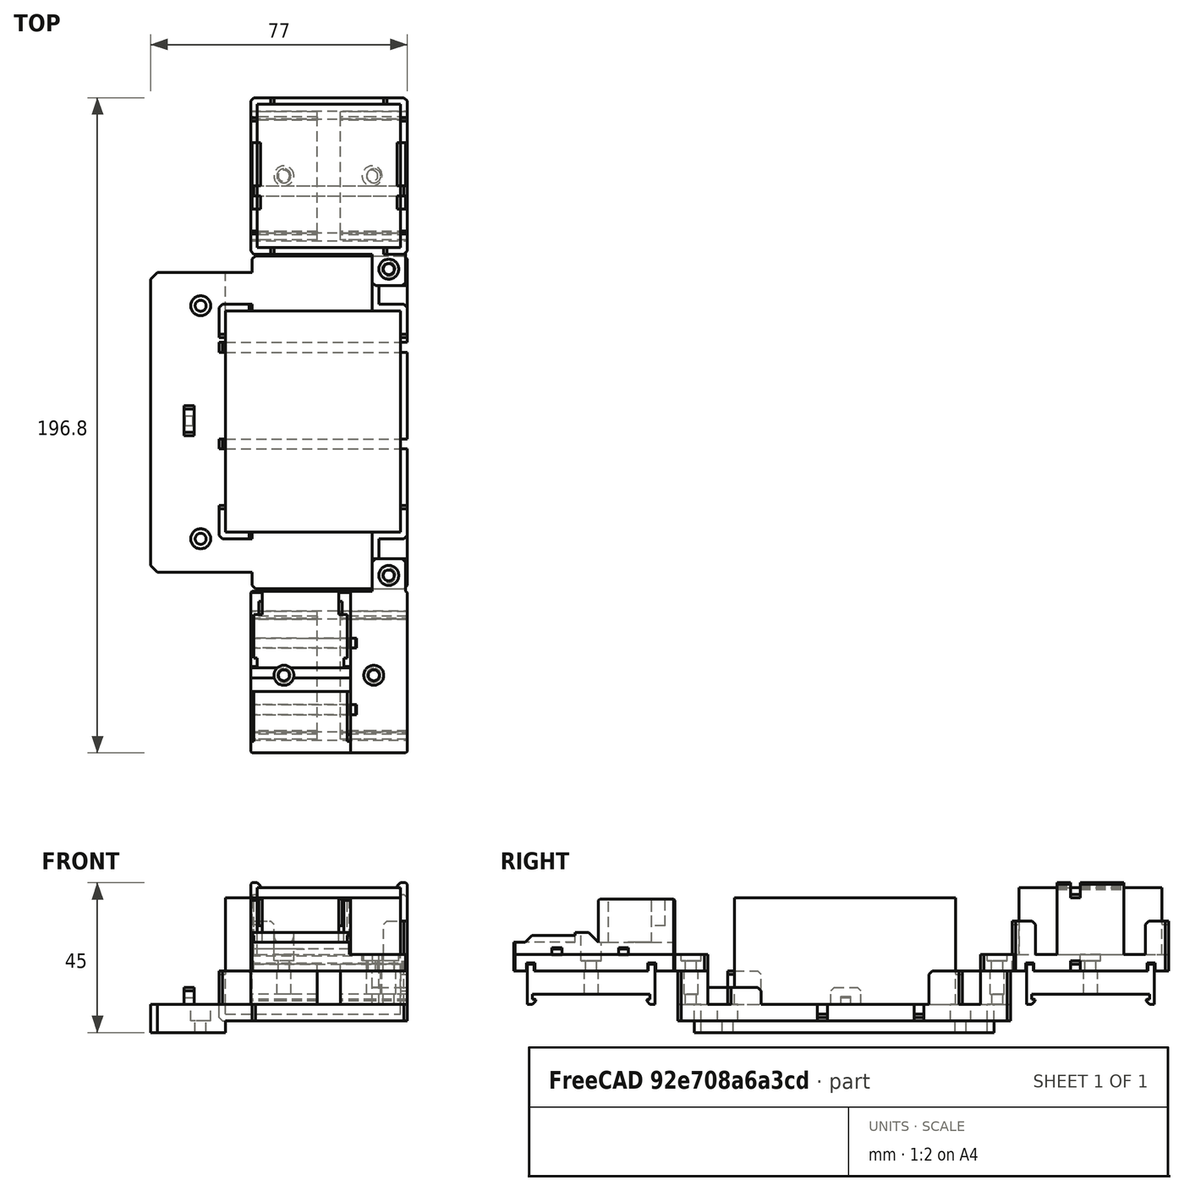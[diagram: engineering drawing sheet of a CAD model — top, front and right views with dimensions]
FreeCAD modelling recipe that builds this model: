
FCSTD DOCUMENT  (FreeCAD 0.18R16146 (Git))
Label: mini-power-power-mount
License: All rights reserved
LicenseURL: http://en.wikipedia.org/wiki/All_rights_reserved
objects: Part::Box×49, Part::MultiFuse×41, Part::Chamfer×32, Part::Cylinder×22, Part::Cut×18, Part::Feature×6
note: 168 computed .brp shape members not serialized (recipe doc carries the construction recipe); baked Part::Feature solids carry a one-line shape summary decoded from their .brp

FEATURE [Part::Feature] Cut003001  label="din-mount"
  Placement = pos=(23.5,-18,-10) rot=(0,-1,0;1.5708rad)
  shape: bbox 20 x 38.4 x 12 mm, 68 faces (baked)
FEATURE [Part::Box] Box  label="sonoff-pos"
  AttacherType = Attacher::AttachEngine3D
  Height = 20
  Length = 43
  Placement = pos=(-21.5,-21.5,0) rot=(0,0,1;0rad)
  Width = 43
FEATURE [Part::Box] Box001  label="Cube"
  AttacherType = Attacher::AttachEngine3D
  Height = 10
  Length = 7
  Placement = pos=(-23.5,21.5,0) rot=(0,0,1;0rad)
  Width = 2
FEATURE [Part::Box] Box002  label="Cube001"
  AttacherType = Attacher::AttachEngine3D
  Height = 10
  Length = 7
  Placement = pos=(16.5,21.5,0) rot=(0,0,1;0rad)
  Width = 2
FEATURE [Part::Box] Box003  label="Cube002"
  AttacherType = Attacher::AttachEngine3D
  Height = 10
  Length = 7
  Placement = pos=(-23.5,-23.5,0) rot=(0,0,1;0rad)
  Width = 2
FEATURE [Part::Box] Box004  label="Cube003"
  AttacherType = Attacher::AttachEngine3D
  Height = 10
  Length = 7
  Placement = pos=(16.5,-23.5,0) rot=(0,0,1;0rad)
  Width = 2
FEATURE [Part::Box] Box005  label="Cube004"
  AttacherType = Attacher::AttachEngine3D
  Height = 10
  Length = 2
  Placement = pos=(-23.5,-23.5,0) rot=(0,0,1;0rad)
  Width = 7
FEATURE [Part::Box] Box006  label="Cube005"
  AttacherType = Attacher::AttachEngine3D
  Height = 10
  Length = 2
  Placement = pos=(21.5,-23.5,0) rot=(0,0,1;0rad)
  Width = 7
FEATURE [Part::Box] Box007  label="Cube006"
  AttacherType = Attacher::AttachEngine3D
  Height = 10
  Length = 2
  Placement = pos=(21.5,16.5,0) rot=(0,0,1;0rad)
  Width = 7
FEATURE [Part::Box] Box008  label="Cube007"
  AttacherType = Attacher::AttachEngine3D
  Height = 10
  Length = 2
  Placement = pos=(-23.5,16.5,0) rot=(0,0,1;0rad)
  Width = 7
FEATURE [Part::Feature] Cut003002  label="din-mount001"
  Placement = pos=(-3.5,-18,-10) rot=(0,-1,0;1.5708rad)
  shape: bbox 20 x 38.4 x 12 mm, 68 faces (baked)
FEATURE [Part::Box] Box009  label="Cube008"
  AttacherType = Attacher::AttachEngine3D
  Height = 20
  Length = 2
  Placement = pos=(-23.5,-10,0) rot=(0,0,1;0rad)
  Width = 20
FEATURE [Part::Box] Box010  label="Cube009"
  AttacherType = Attacher::AttachEngine3D
  Height = 20
  Length = 2
  Placement = pos=(21.5,-10,0) rot=(0,0,1;0rad)
  Width = 20
FEATURE [Part::Box] Box011  label="Cube010"
  AttacherType = Attacher::AttachEngine3D
  Height = 2
  Length = 3
  Placement = pos=(-23.5,-10,19.5) rot=(0,0,1;0rad)
  Width = 20
FEATURE [Part::Box] Box012  label="Cube011"
  AttacherType = Attacher::AttachEngine3D
  Height = 2
  Length = 3
  Placement = pos=(20.5,-10,19.5) rot=(0,0,1;0rad)
  Width = 20
FEATURE [Part::Chamfer] Chamfer
  Base = -> Box011
  Edges = 1 edges r=1: [Edge6]
FEATURE [Part::Chamfer] Chamfer001
  Base = -> Box012
  Edges = 1 edges r=1: [Edge2]
FEATURE [Part::Chamfer] Chamfer002
  Base = -> Chamfer
  Edges = 1 edges: [Edge3 r1=0.5 r2=1]
FEATURE [Part::Chamfer] Chamfer003
  Base = -> Chamfer001
  Edges = 1 edges: [Edge3 r1=0.5 r2=1]
FEATURE [Part::Chamfer] Chamfer004
  Base = -> Chamfer002
  Edges = 1 edges r=0.5: [Edge18]
FEATURE [Part::Chamfer] Chamfer005
  Base = -> Chamfer003
  Edges = 1 edges r=0.5: [Edge18]
FEATURE [Part::MultiFuse] Fusion
  Shapes = -> [Box009,Chamfer004]
FEATURE [Part::MultiFuse] Fusion001
  Shapes = -> [Box010,Chamfer005]
FEATURE [Part::MultiFuse] Fusion002
  Shapes = -> [Box008,Box001]
FEATURE [Part::MultiFuse] Fusion003
  Shapes = -> [Box002,Box007]
FEATURE [Part::MultiFuse] Fusion004
  Shapes = -> [Box005,Box003]
FEATURE [Part::MultiFuse] Fusion005
  Shapes = -> [Box004,Box006]
FEATURE [Part::Chamfer] Chamfer006
  Base = -> Fusion002
  Edges = 1 edges r=1: [Edge9]
FEATURE [Part::Chamfer] Chamfer007
  Base = -> Fusion004
  Edges = 1 edges r=1: [Edge1]
FEATURE [Part::Chamfer] Chamfer008
  Base = -> Fusion005
  Edges = 1 edges r=1: [Edge14]
FEATURE [Part::Chamfer] Chamfer009
  Base = -> Fusion003
  Edges = 1 edges r=1: [Edge20]
FEATURE [Part::Box] Box013  label="Cube012"
  AttacherType = Attacher::AttachEngine3D
  Height = 5
  Length = 47
  Placement = pos=(-23.5,-23.5,-5) rot=(0,0,1;0rad)
  Width = 47
FEATURE [Part::MultiFuse] Fusion006  label="din-pos"
  Placement = pos=(0,0.3,-2) rot=(0,0,1;0rad)
  Shapes = -> [Cut003001,Cut003002]
FEATURE [Part::Cylinder] Cylinder
  Angle = 360
  AttacherType = Attacher::AttachEngine3D
  Height = 10
  Placement = pos=(-13.5,0,0) rot=(0,0,1;0rad)
  Radius = 3
FEATURE [Part::Cylinder] Cylinder001
  Angle = 360
  AttacherType = Attacher::AttachEngine3D
  Height = 10
  Placement = pos=(13,0,0) rot=(0,0,1;0rad)
  Radius = 3
FEATURE [Part::Cylinder] Cylinder002
  Angle = 360
  AttacherType = Attacher::AttachEngine3D
  Height = 10
  Placement = pos=(13,0,0) rot=(0,0,1;0rad)
  Radius = 1.7
FEATURE [Part::Cylinder] Cylinder003
  Angle = 360
  AttacherType = Attacher::AttachEngine3D
  Height = 10
  Placement = pos=(-13.5,0,0) rot=(0,0,1;0rad)
  Radius = 1.7
FEATURE [Part::MultiFuse] Fusion007
  Shapes = -> [Cylinder003,Cylinder002]
FEATURE [Part::MultiFuse] Fusion008
  Placement = pos=(0,0,10) rot=(0,0,1;0rad)
  Shapes = -> [Cylinder001,Cylinder]
FEATURE [Part::MultiFuse] Fusion009
  Placement = pos=(0,0,-12) rot=(0,0,1;0rad)
  Shapes = -> [Fusion008,Fusion007]
FEATURE [Part::Chamfer] Chamfer010
  Base = -> Box013
  Edges = 4 edges r=1: [Edge1,Edge3,Edge5,Edge7]
FEATURE [Part::Cut] Cut
  Base = -> Chamfer010
  Tool = -> Fusion009
FEATURE [Part::Box] Box014  label="Cube013"
  AttacherType = Attacher::AttachEngine3D
  Height = 2.4
  Length = 50
  Placement = pos=(-25,-19.45,-5) rot=(0,0,1;0rad)
  Width = 2.4
FEATURE [Part::Box] Box015  label="Cube014"
  AttacherType = Attacher::AttachEngine3D
  Height = 2.4
  Length = 50
  Placement = pos=(-25,17.05,-5) rot=(0,0,1;0rad)
  Width = 2.4
FEATURE [Part::MultiFuse] Fusion010
  Shapes = -> [Fusion,Fusion001,Chamfer006,Chamfer007,Chamfer008,Chamfer009,Cut]
FEATURE [Part::Chamfer] Chamfer011
  Base = -> Fusion010
  Edges = 8 edges r=1: [Edge23,Edge27,Edge90,Edge99,Edge106,Edge122,Edge129,Edge136]
FEATURE [Part::MultiFuse] Fusion011
  Shapes = -> [Box014,Box015]
FEATURE [Part::Cut] Cut003003
  Base = -> Chamfer011
  Tool = -> Fusion011
FEATURE [Part::Cylinder] Cylinder004
  Angle = 360
  AttacherType = Attacher::AttachEngine3D
  Height = 10
  Placement = pos=(18,-28,0) rot=(0,0,1;0rad)
  Radius = 3
FEATURE [Part::Box] Box016  label="Cube015"
  AttacherType = Attacher::AttachEngine3D
  Height = 5
  Length = 10
  Placement = pos=(13,-33,-5) rot=(0,0,1;0rad)
  Width = 10
FEATURE [Part::Cylinder] Cylinder005
  Angle = 360
  AttacherType = Attacher::AttachEngine3D
  Height = 10
  Placement = pos=(18,-28,-7) rot=(0,0,1;0rad)
  Radius = 1.7
FEATURE [Part::MultiFuse] Fusion012
  Placement = pos=(0,0,-2) rot=(0,0,1;0rad)
  Shapes = -> [Cylinder005,Cylinder004]
FEATURE [Part::Cut] Cut003004
  Base = -> Box016
  Tool = -> Fusion012
FEATURE [Part::Chamfer] Chamfer012
  Base = -> Cut003004
  Edges = 2 edges r=1: [Edge1,Edge6]
FEATURE [Part::MultiFuse] Fusion013  label="sonoff-r1"
  Shapes = -> [Cut003003,Chamfer012]
FEATURE [Part::Feature] Fusion006001  label="din-pos001"
  Placement = pos=(0,-149.7,-2) rot=(0,0,1;0rad)
  shape: bbox 47 x 38.4 x 12 mm, 136 faces, 2 solids (baked)
FEATURE [Part::Feature] Chamfer005001  label="power-connector-mount"
  Placement = pos=(6.5,-149.3,-0.4) rot=(0,0,1;3.14159rad)
  shape: bbox 30 x 48.5 x 17 mm, 71 faces (baked)
FEATURE [Part::Box] Box017  label="Cube016"
  AttacherType = Attacher::AttachEngine3D
  Height = 5
  Length = 47
  Placement = pos=(-23.5,-173.3,-5) rot=(0,0,1;0rad)
  Width = 48.5
FEATURE [Part::Chamfer] Chamfer005002
  Base = -> Box017
  Edges = 4 edges r=0.4: [Edge1,Edge3,Edge5,Edge7]
FEATURE [Part::MultiFuse] Fusion006002
  Shapes = -> [Chamfer005002,Chamfer005001]
FEATURE [Part::Cylinder] Cylinder006
  Angle = 360
  AttacherType = Attacher::AttachEngine3D
  Height = 15
  Placement = pos=(-13.5,-150,0) rot=(0,0,1;0rad)
  Radius = 1.65
FEATURE [Part::Cylinder] Cylinder007
  Angle = 360
  AttacherType = Attacher::AttachEngine3D
  Height = 15
  Placement = pos=(13.5,-150,0) rot=(0,0,1;0rad)
  Radius = 1.65
FEATURE [Part::Cylinder] Cylinder008
  Angle = 360
  AttacherType = Attacher::AttachEngine3D
  Height = 15
  Placement = pos=(-13.5,-150,0) rot=(0,0,1;0rad)
  Radius = 3
FEATURE [Part::Cylinder] Cylinder009
  Angle = 360
  AttacherType = Attacher::AttachEngine3D
  Height = 15
  Placement = pos=(13.5,-150,0) rot=(0,0,1;0rad)
  Radius = 3
FEATURE [Part::MultiFuse] Fusion006003
  Placement = pos=(0,0,13) rot=(0,0,1;0rad)
  Shapes = -> [Cylinder009,Cylinder008]
FEATURE [Part::MultiFuse] Fusion006004
  Shapes = -> [Cylinder007,Cylinder006]
FEATURE [Part::MultiFuse] Fusion006005
  Placement = pos=(0,0,-15) rot=(0,0,1;0rad)
  Shapes = -> [Fusion006003,Fusion006004]
FEATURE [Part::Cylinder] Cylinder010
  Angle = 360
  AttacherType = Attacher::AttachEngine3D
  Height = 4
  Placement = pos=(-8.5,-135,-0.4) rot=(0,0,1;0rad)
  Radius = 4
FEATURE [Part::Cylinder] Cylinder011
  Angle = 360
  AttacherType = Attacher::AttachEngine3D
  Height = 4
  Placement = pos=(-8.5,-154.5,-0.4) rot=(0,0,1;0rad)
  Radius = 4
FEATURE [Part::Box] Box018  label="Cube017"
  AttacherType = Attacher::AttachEngine3D
  Height = 6
  Length = 10
  Placement = pos=(-13.5,-154.8,0.6) rot=(0,0,1;0rad)
  Width = 4
FEATURE [Part::MultiFuse] Fusion006006
  Shapes = -> [Fusion006002,Cylinder010,Cylinder011,Box018]
FEATURE [Part::Cut] Cut003005
  Base = -> Fusion006006
  Tool = -> Fusion006005
FEATURE [Part::Box] Box019  label="Cube018"
  AttacherType = Attacher::AttachEngine3D
  Height = 2
  Length = 50
  Placement = pos=(-25,-141.8,-0.4) rot=(0,0,1;0rad)
  Width = 3
FEATURE [Part::Box] Box020  label="Cube019"
  AttacherType = Attacher::AttachEngine3D
  Height = 2
  Length = 50
  Placement = pos=(-25,-161.8,-0.4) rot=(0,0,1;0rad)
  Width = 3
FEATURE [Part::Box] Box021  label="Cube020"
  AttacherType = Attacher::AttachEngine3D
  Height = 2.4
  Length = 50
  Placement = pos=(-25,-133.05,-5) rot=(0,0,1;0rad)
  Width = 2.5
FEATURE [Part::MultiFuse] Fusion006007
  Placement = pos=(-17,0,0) rot=(0,0,1;0rad)
  Shapes = -> [Box019,Box020]
FEATURE [Part::Cut] Cut003006
  Base = -> Cut003005
  Tool = -> Fusion006007
FEATURE [Part::Chamfer] Chamfer005003
  Base = -> Cut003006
  Edges = 2 edges r=0.3: [Edge143,Edge146]
FEATURE [Part::Chamfer] Chamfer005004
  Base = -> Chamfer005003
  Edges = 4 edges r=0.4: [Edge30,Edge33,Edge97,Edge103]
FEATURE [Part::Box] Box022  label="Cube021"
  AttacherType = Attacher::AttachEngine3D
  Height = 2.4
  Length = 50
  Placement = pos=(-25,-169.45,-5) rot=(0,0,1;0rad)
  Width = 2.5
FEATURE [Part::Cut] Cut003007
  Base = -> Chamfer005004
  Tool = -> Box021
FEATURE [Part::Cut] Cut003008
  Base = -> Cut003007
  Tool = -> Box022
FEATURE [Part::Cylinder] Cylinder012
  Angle = 360
  AttacherType = Attacher::AttachEngine3D
  Height = 10
  Placement = pos=(18,-121,0) rot=(0,0,1;0rad)
  Radius = 3
FEATURE [Part::Cylinder] Cylinder013
  Angle = 360
  AttacherType = Attacher::AttachEngine3D
  Height = 10
  Placement = pos=(18,-121,-7) rot=(0,0,1;0rad)
  Radius = 1.65
FEATURE [Part::MultiFuse] Fusion006008
  Placement = pos=(0,0,-2) rot=(0,0,1;0rad)
  Shapes = -> [Cylinder013,Cylinder012]
FEATURE [Part::Box] Box023  label="Cube022"
  AttacherType = Attacher::AttachEngine3D
  Height = 5
  Length = 10
  Placement = pos=(13,-126,-5) rot=(0,0,1;0rad)
  Width = 10
FEATURE [Part::Chamfer] Chamfer005005
  Base = -> Box023
  Edges = 2 edges r=1: [Edge3,Edge7]
FEATURE [Part::Cut] Cut003009
  Base = -> Chamfer005005
  Placement = pos=(0,1,0) rot=(0,0,1;0rad)
  Tool = -> Fusion006008
FEATURE [Part::MultiFuse] Fusion006009  label="plug-r1"
  Shapes = -> [Cut003008,Cut003009]
FEATURE [Part::Box] Box024  label="Cube023"
  AttacherType = Attacher::AttachEngine3D
  Height = 2
  Length = 50
  Placement = pos=(-25,-6,-5) rot=(0,0,1;0rad)
  Width = 3
FEATURE [Part::Box] Box025  label="Cube024"
  AttacherType = Attacher::AttachEngine3D
  Height = 5
  Length = 50
  Placement = pos=(-25,-6,18) rot=(0,0,1;0rad)
  Width = 3
FEATURE [Part::Cut] Cut003010
  Base = -> Fusion013
  Tool = -> Box024
FEATURE [Part::Chamfer] Chamfer005006
  Base = -> Cut003010
  Edges = 2 edges r=1: [Edge28,Edge98]
FEATURE [Part::Cut] Cut003011
  Base = -> Chamfer005006
  Tool = -> Box025
FEATURE [Part::Chamfer] Chamfer005007  label="sonoff-r1-f1"
  Base = -> Cut003011
  Edges = 2 edges r=1: [Edge112,Edge255]
FEATURE [Part::Cylinder] Cylinder014
  Angle = 360
  AttacherType = Attacher::AttachEngine3D
  Height = 20
  Placement = pos=(18,-28,0) rot=(0,0,1;0rad)
  Radius = 1.65
FEATURE [Part::Cylinder] Cylinder015
  Angle = 360
  AttacherType = Attacher::AttachEngine3D
  Height = 20
  Placement = pos=(18,-120,0) rot=(0,0,1;0rad)
  Radius = 1.65
FEATURE [Part::Cylinder] Cylinder016
  Angle = 360
  AttacherType = Attacher::AttachEngine3D
  Height = 10
  Placement = pos=(-38.5,-34,0) rot=(0,0,1;0rad)
  Radius = 1.65
FEATURE [Part::Box] Box026  label="Cube025"
  AttacherType = Attacher::AttachEngine3D
  Height = 32
  Length = 52.5
  Placement = pos=(-31,-107,-15) rot=(0,0,1;0rad)
  Width = 66.5
FEATURE [Part::Box] Box027  label="Cube026"
  AttacherType = Attacher::AttachEngine3D
  Height = 5
  Length = 77
  Placement = pos=(-53.5,-124,-20) rot=(0,0,1;0rad)
  Width = 100
FEATURE [Part::Box] Box028  label="Cube027"
  AttacherType = Attacher::AttachEngine3D
  Height = 10
  Length = 10.5
  Placement = pos=(13,-33,-15) rot=(0,0,1;0rad)
  Width = 9
FEATURE [Part::Box] Box029  label="Cube028"
  AttacherType = Attacher::AttachEngine3D
  Height = 10
  Length = 10.5
  Placement = pos=(13,-124,-15) rot=(0,0,1;0rad)
  Width = 9
FEATURE [Part::Box] Box030  label="Cube029"
  AttacherType = Attacher::AttachEngine3D
  Height = 10
  Length = 10
  Placement = pos=(13.5,-40.5,-15) rot=(0,0,1;0rad)
  Width = 2
FEATURE [Part::Box] Box031  label="Cube030"
  AttacherType = Attacher::AttachEngine3D
  Height = 10
  Length = 10
  Placement = pos=(-33,-40.5,-15) rot=(0,0,1;0rad)
  Width = 2
FEATURE [Part::Box] Box032  label="Cube031"
  AttacherType = Attacher::AttachEngine3D
  Height = 10
  Length = 10
  Placement = pos=(-33,-109,-15) rot=(0,0,1;0rad)
  Width = 2
FEATURE [Part::Box] Box033  label="Cube032"
  AttacherType = Attacher::AttachEngine3D
  Height = 5
  Length = 10
  Placement = pos=(13.5,-109,-15) rot=(0,0,1;0rad)
  Width = 2
FEATURE [Part::Box] Box034  label="Cube033"
  AttacherType = Attacher::AttachEngine3D
  Height = 10
  Length = 2
  Placement = pos=(-33,-48.5,-15) rot=(0,0,1;0rad)
  Width = 10
FEATURE [Part::Box] Box035  label="Cube034"
  AttacherType = Attacher::AttachEngine3D
  Height = 10
  Length = 2
  Placement = pos=(21.5,-48.5,-15) rot=(0,0,1;0rad)
  Width = 10
FEATURE [Part::Box] Box036  label="Cube035"
  AttacherType = Attacher::AttachEngine3D
  Height = 5
  Length = 2
  Placement = pos=(21.5,-107,-15) rot=(0,0,1;0rad)
  Width = 8
FEATURE [Part::Box] Box037  label="Cube036"
  AttacherType = Attacher::AttachEngine3D
  Height = 10
  Length = 2
  Placement = pos=(-33,-109,-15) rot=(0,0,1;0rad)
  Width = 10
FEATURE [Part::MultiFuse] Fusion006010
  Shapes = -> [Box037,Box032]
FEATURE [Part::Chamfer] Chamfer005009
  Base = -> Fusion006010
  Edges = 3 edges r=1: [Edge1,Edge18,Edge21]
FEATURE [Part::MultiFuse] Fusion006013
  Shapes = -> [Box034,Box031]
FEATURE [Part::Chamfer] Chamfer005012
  Base = -> Fusion006013
  Edges = 3 edges r=1: [Edge7,Edge9,Edge22]
FEATURE [Part::Box] Box038  label="Cube037"
  AttacherType = Attacher::AttachEngine3D
  Height = 10
  Length = 2
  Placement = pos=(13,-40.5,-15) rot=(0,0,1;0rad)
  Width = 16.5
FEATURE [Part::Box] Box039  label="Cube038"
  AttacherType = Attacher::AttachEngine3D
  Height = 5
  Length = 2
  Placement = pos=(13,-124,-15) rot=(0,0,1;0rad)
  Width = 17
FEATURE [Part::MultiFuse] Fusion006015
  Shapes = -> [Box030,Box035]
FEATURE [Part::Chamfer] Chamfer005014
  Base = -> Fusion006015
  Edges = 2 edges r=1: [Edge20,Edge24]
FEATURE [Part::MultiFuse] Fusion006016
  Shapes = -> [Box038,Box028]
FEATURE [Part::Chamfer] Chamfer005015
  Base = -> Fusion006016
  Edges = 1 edges r=1: [Edge27]
FEATURE [Part::MultiFuse] Fusion006017
  Shapes = -> [Box033,Box036]
FEATURE [Part::Chamfer] Chamfer005016
  Base = -> Fusion006017
  Edges = 2 edges r=1: [Edge6,Edge17]
FEATURE [Part::Chamfer] Chamfer005017
  Base = -> Box029
  Edges = 1 edges r=1: [Edge5]
FEATURE [Part::MultiFuse] Fusion006018
  Shapes = -> [Box039,Chamfer005016,Chamfer005017]
FEATURE [Part::MultiFuse] Fusion006019
  Shapes = -> [Chamfer005015,Chamfer005014]
FEATURE [Part::MultiFuse] Fusion006020
  Shapes = -> [Chamfer005009,Fusion006018,Fusion006019,Chamfer005012]
FEATURE [Part::Cylinder] Cylinder017
  Angle = 360
  AttacherType = Attacher::AttachEngine3D
  Height = 7
  Placement = pos=(18,-28,0) rot=(0,0,1;0rad)
  Radius = 2.1
FEATURE [Part::Cylinder] Cylinder018
  Angle = 360
  AttacherType = Attacher::AttachEngine3D
  Height = 7
  Placement = pos=(18,-120,0) rot=(0,0,1;0rad)
  Radius = 2.1
FEATURE [Part::MultiFuse] Fusion006021
  Placement = pos=(0,0,-23) rot=(0,0,1;0rad)
  Shapes = -> [Cylinder014,Cylinder015]
FEATURE [Part::Cut] Cut003012
  Base = -> Fusion006020
  Tool = -> Fusion006021
FEATURE [Part::MultiFuse] Fusion006022
  Placement = pos=(0,0,-12) rot=(0,0,1;0rad)
  Shapes = -> [Cylinder018,Cylinder017]
FEATURE [Part::Cut] Cut003013
  Base = -> Cut003012
  Tool = -> Fusion006022
FEATURE [Part::Box] Box040  label="Cube039"
  AttacherType = Attacher::AttachEngine3D
  Height = 2
  Length = 57
  Placement = pos=(-33,-82,-20) rot=(0,0,1;0rad)
  Width = 3
FEATURE [Part::Box] Box041  label="Cube040"
  AttacherType = Attacher::AttachEngine3D
  Height = 2
  Length = 57
  Placement = pos=(-33,-53,-20) rot=(0,0,1;0rad)
  Width = 3
FEATURE [Part::Box] Box042  label="Cube041"
  AttacherType = Attacher::AttachEngine3D
  Height = 53
  Length = 2
  Placement = pos=(-33,-53,-20) rot=(0,0,1;0rad)
  Width = 3
FEATURE [Part::Box] Box043  label="Cube042"
  AttacherType = Attacher::AttachEngine3D
  Height = 53
  Length = 2
  Placement = pos=(-33,-82,-20) rot=(0,0,1;0rad)
  Width = 3
FEATURE [Part::MultiFuse] Fusion006023
  Shapes = -> [Box043,Box042]
FEATURE [Part::MultiFuse] Fusion006024
  Shapes = -> [Box041,Box040]
FEATURE [Part::Feature] Fusion006023001  label="Fusion006025"
  Placement = pos=(54.5,0,0) rot=(0,0,1;0rad)
  shape: bbox 2 x 32 x 53 mm, 12 faces, 2 solids (baked)
FEATURE [Part::Cylinder] Cylinder019
  Angle = 360
  AttacherType = Attacher::AttachEngine3D
  Height = 10
  Placement = pos=(-38.5,-114,0) rot=(0,0,1;0rad)
  Radius = 1.65
FEATURE [Part::Cylinder] Cylinder020
  Angle = 360
  AttacherType = Attacher::AttachEngine3D
  Height = 10
  Placement = pos=(-38.5,-114,10) rot=(0,0,1;0rad)
  Radius = 3
FEATURE [Part::Cylinder] Cylinder021
  Angle = 360
  AttacherType = Attacher::AttachEngine3D
  Height = 10
  Placement = pos=(-38.5,-34,10) rot=(0,0,1;0rad)
  Radius = 3
FEATURE [Part::Box] Box044  label="Cube043"
  AttacherType = Attacher::AttachEngine3D
  Height = 5
  Length = 30.5
  Placement = pos=(-53.5,-29,-20) rot=(0,0,1;0rad)
  Width = 5
FEATURE [Part::Box] Box045  label="Cube044"
  AttacherType = Attacher::AttachEngine3D
  Height = 5
  Length = 30.5
  Placement = pos=(-53.5,-124,-20) rot=(0,0,1;0rad)
  Width = 5
FEATURE [Part::MultiFuse] Fusion006023004
  Shapes = -> [Box045,Box044]
FEATURE [Part::Cut] Cut003014
  Base = -> Box027
  Tool = -> Fusion006023004
FEATURE [Part::Box] Box046  label="Cube045"
  AttacherType = Attacher::AttachEngine3D
  Height = 3.5
  Length = 22.5
  Placement = pos=(-53.5,-119,-23.5) rot=(0,0,1;0rad)
  Width = 90
FEATURE [Part::Chamfer] Chamfer005018
  Base = -> Cut003014
  Edges = 2 edges r=1: [Edge23,Edge24]
FEATURE [Part::Chamfer] Chamfer005019
  Base = -> Chamfer005018
  Edges = 2 edges r=2: [Edge21,Edge24]
FEATURE [Part::Chamfer] Chamfer005020
  Base = -> Box046
  Edges = 2 edges r=2: [Edge1,Edge3]
FEATURE [Part::Cut] Cut003015
  Base = -> Chamfer005019
  Tool = -> Fusion006023
FEATURE [Part::Cut] Cut003016
  Base = -> Cut003015
  Tool = -> Fusion006023001
FEATURE [Part::Cut] Cut003017
  Base = -> Cut003016
  Tool = -> Fusion006024
FEATURE [Part::MultiFuse] Fusion006023005
  Shapes = -> [Cut003017,Cut003013]
FEATURE [Part::MultiFuse] Fusion006023006
  Placement = pos=(0,-5,0) rot=(0,0,1;0rad)
  Shapes = -> [Cylinder016,Cylinder021]
FEATURE [Part::MultiFuse] Fusion006023007
  Placement = pos=(0,5,0) rot=(0,0,1;0rad)
  Shapes = -> [Cylinder019,Cylinder020]
FEATURE [Part::MultiFuse] Fusion006023008
  Placement = pos=(0,0,-30) rot=(0,0,1;0rad)
  Shapes = -> [Fusion006023006,Fusion006023007]
FEATURE [Part::MultiFuse] Fusion006023009
  Shapes = -> [Fusion006023005,Chamfer005020]
FEATURE [Part::Cut] Cut003018
  Base = -> Fusion006023009
  Tool = -> Fusion006023008
FEATURE [Part::Chamfer] Chamfer005021
  Base = -> Cut003018
  Edges = 2 edges r=1: [Edge311,Edge323]
FEATURE [Part::Chamfer] Chamfer005022
  Base = -> Chamfer005021
  Edges = 2 edges r=1: [Edge106,Edge124]
FEATURE [Part::Box] Box047  label="Cube046"
  AttacherType = Attacher::AttachEngine3D
  Height = 2
  Length = 3
  Placement = pos=(-43.5,-75,-15) rot=(0,0,1;0rad)
  Width = 3
FEATURE [Part::Box] Box048  label="Cube047"
  AttacherType = Attacher::AttachEngine3D
  Height = 5
  Length = 3
  Placement = pos=(-43.5,-78,-15) rot=(0,0,1;0rad)
  Width = 9
FEATURE [Part::Cut] Cut003019
  Base = -> Box048
  Tool = -> Box047
FEATURE [Part::Chamfer] Chamfer005023
  Base = -> Cut003019
  Edges = 2 edges r=1: [Edge9,Edge11]
FEATURE [Part::Chamfer] Chamfer005024
  Base = -> Chamfer005023
  Edges = 2 edges r=0.4: [Edge10,Edge30]
FEATURE [Part::MultiFuse] Fusion006023010
  Shapes = -> [Chamfer005024,Chamfer005022]
FEATURE [Part::Feature] Chamfer005007001  label="sonoff-r1-f002"
  shape: bbox 47 x 56.5 x 26.5 mm, 101 faces (baked)
